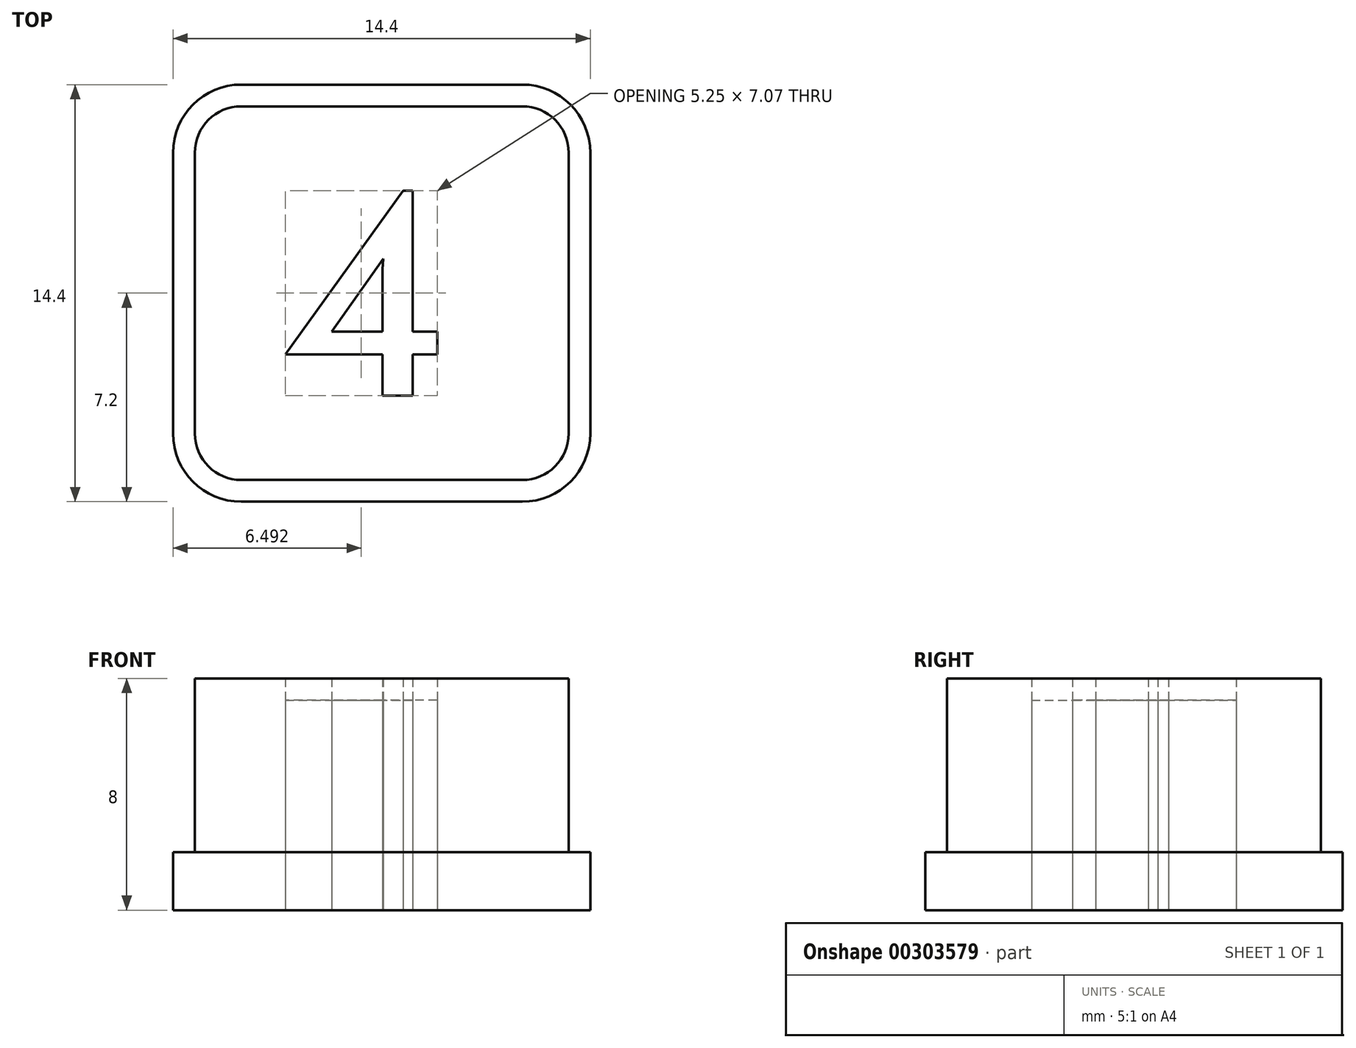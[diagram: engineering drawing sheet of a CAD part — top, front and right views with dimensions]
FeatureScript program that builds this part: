
annotation { "Feature Type Name" : "Feature", "Feature Type Description" : "" }
export const myFeature = defineFeature(function(context is Context, id is Id, definition is map)
    precondition{}
    {
        {
            var Q0;
            Q0=qCreatedBy(makeId("Top.planeOp"),FACE);
            var sketch = newSketch(context, id + "F0", { "sketchPlane" : qUnion([Q0])});
            skArc(sketch, "E0", {"start": v(4.85, -6.45) * mm, "mid": v(5.98, -5.98) * mm, "end": v(6.45, -4.85) * mm});
            skLineSegment(sketch, "E1", {"start": v(6.45, -4.85) * mm, "end": v(6.45, 4.85) * mm});
            skArc(sketch, "E2", {"start": v(6.45, 4.85) * mm, "mid": v(5.98, 5.98) * mm, "end": v(4.85, 6.45) * mm});
            skLineSegment(sketch, "E3", {"start": v(4.85, 6.45) * mm, "end": v(-4.85, 6.45) * mm});
            skArc(sketch, "E4", {"start": v(-4.85, 6.45) * mm, "mid": v(-5.98, 5.98) * mm, "end": v(-6.45, 4.85) * mm});
            skLineSegment(sketch, "E5", {"start": v(-6.45, 4.85) * mm, "end": v(-6.45, -4.85) * mm});
            skArc(sketch, "E6", {"start": v(-6.45, -4.85) * mm, "mid": v(-5.98, -5.98) * mm, "end": v(-4.85, -6.45) * mm});
            skLineSegment(sketch, "E7", {"start": v(-4.85, -6.45) * mm, "end": v(4.85, -6.45) * mm});
            skArc(sketch, "E8", {"start": v(-4.85, 7.2) * mm, "mid": v(-6.51, 6.51) * mm, "end": v(-7.2, 4.85) * mm});
            skLineSegment(sketch, "E9", {"start": v(-7.2, 4.85) * mm, "end": v(-7.2, -4.85) * mm});
            skArc(sketch, "E10", {"start": v(-7.2, -4.85) * mm, "mid": v(-6.51, -6.51) * mm, "end": v(-4.85, -7.2) * mm});
            skLineSegment(sketch, "E11", {"start": v(-4.85, -7.2) * mm, "end": v(4.85, -7.2) * mm});
            skArc(sketch, "E12", {"start": v(4.85, -7.2) * mm, "mid": v(6.51, -6.51) * mm, "end": v(7.2, -4.85) * mm});
            skLineSegment(sketch, "E13", {"start": v(7.2, -4.85) * mm, "end": v(7.2, 4.85) * mm});
            skArc(sketch, "E14", {"start": v(7.2, 4.85) * mm, "mid": v(6.51, 6.51) * mm, "end": v(4.85, 7.2) * mm});
            skLineSegment(sketch, "E15", {"start": v(4.85, 7.2) * mm, "end": v(-4.85, 7.2) * mm});
            skLineSegment(sketch, "E16", {"start": v(0.05, 1.2) * mm, "end": v(-1.73, -1.32) * mm});
            skLineSegment(sketch, "E17", {"start": v(-1.73, -1.32) * mm, "end": v(0.03, -1.32) * mm});
            skLineSegment(sketch, "E18", {"start": v(0.03, -1.32) * mm, "end": v(0.03, 0.5) * mm});
            skLineSegment(sketch, "E19", {"start": v(0.03, 0.5) * mm, "end": v(0.03, 0.82) * mm});
            skLineSegment(sketch, "E20", {"start": v(0.03, 0.82) * mm, "end": v(0.05, 1.2) * mm});
            skLineSegment(sketch, "E21", {"start": v(0.03, -3.54) * mm, "end": v(0.03, -2.12) * mm});
            skLineSegment(sketch, "E22", {"start": v(0.03, -2.12) * mm, "end": v(-3.33, -2.12) * mm});
            skLineSegment(sketch, "E23", {"start": v(-3.33, -2.12) * mm, "end": v(0.74, 3.54) * mm});
            skLineSegment(sketch, "E24", {"start": v(0.74, 3.54) * mm, "end": v(1.06, 3.54) * mm});
            skLineSegment(sketch, "E25", {"start": v(1.06, 3.54) * mm, "end": v(1.06, -1.32) * mm});
            skLineSegment(sketch, "E26", {"start": v(1.06, -1.32) * mm, "end": v(1.91, -1.32) * mm});
            skLineSegment(sketch, "E27", {"start": v(1.91, -1.32) * mm, "end": v(1.91, -2.12) * mm});
            skLineSegment(sketch, "E28", {"start": v(1.91, -2.12) * mm, "end": v(1.06, -2.12) * mm});
            skLineSegment(sketch, "E29", {"start": v(1.06, -2.12) * mm, "end": v(1.06, -3.54) * mm});
            skLineSegment(sketch, "E30", {"start": v(1.06, -3.54) * mm, "end": v(0.03, -3.54) * mm});
            skSolve(sketch);
        }
        {
            var Q0;
            Q0=makeQuery(id+"F0.imprint","IMPRINT",FACE,{"disambiguationData":[TD([[makeQuery(id+"F0.imprint","IMPRINT",EDGE,{"derivedFrom":sQuery(id+"F0.wireOp",EDGE,"E0")}),-1.0]])]});
            extrude(context, id + "F1", {"entities" : qUnion([Q0]), "depth" : 2 * mm});
        }
        {
            var Q0;
            Q0=makeQuery(id+"F0.imprint","IMPRINT",FACE,{"disambiguationData":[TD([[makeQuery(id+"F0.imprint","IMPRINT",EDGE,{"derivedFrom":sQuery(id+"F0.wireOp",EDGE,"E0")}),1.0]])]});
            extrude(context, id + "F2", {"entities" : qUnion([Q0]), "operationType" : NewBodyOperationType.ADD, "depth" : 8 * mm});
        }
        {
            var Q0;
            Q0=makeQuery(id+"F0.imprint","IMPRINT",FACE,{"disambiguationData":[TD([[makeQuery(id+"F0.imprint","IMPRINT",EDGE,{"derivedFrom":sQuery(id+"F0.wireOp",EDGE,"E16")}),1.0]])]});
            extrude(context, id + "F3", {"entities" : qUnion([Q0]), "depth" : 8 * mm});
        }
        {
            var Q0;
            Q0=makeQuery(id+"F0.imprint","IMPRINT",FACE,{"disambiguationData":[TD([[makeQuery(id+"F0.imprint","IMPRINT",EDGE,{"derivedFrom":sQuery(id+"F0.wireOp",EDGE,"E16")}),-1.0]])]});
            extrude(context, id + "F4", {"entities" : qUnion([Q0]), "depth" : 7.25 * mm});
        }
    });
